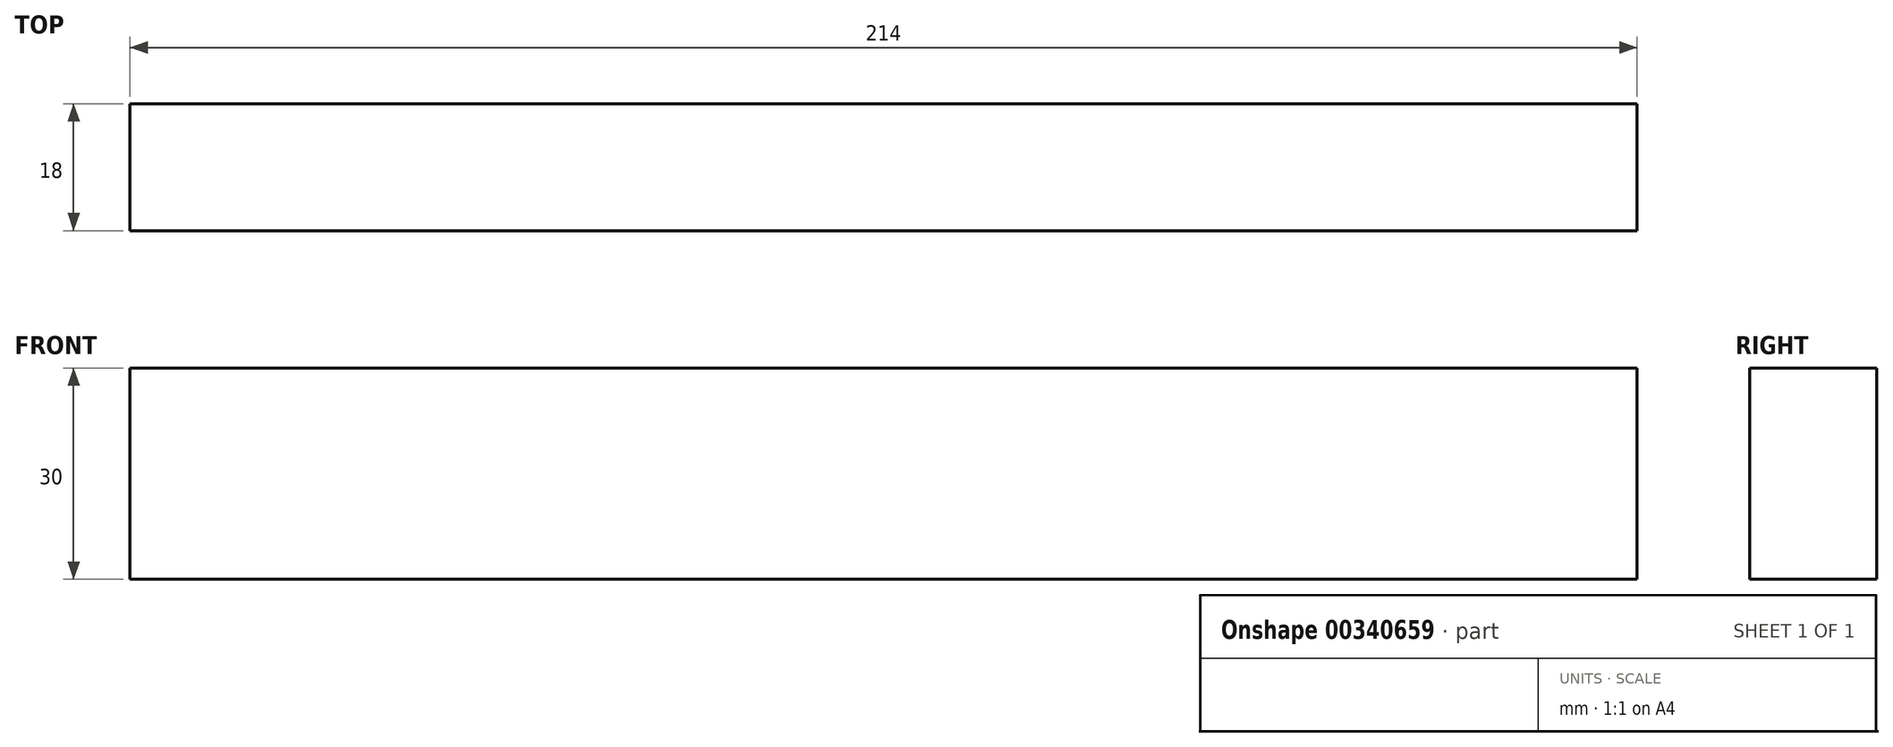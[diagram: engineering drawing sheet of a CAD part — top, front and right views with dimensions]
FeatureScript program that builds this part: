
annotation { "Feature Type Name" : "Feature", "Feature Type Description" : "" }
export const myFeature = defineFeature(function(context is Context, id is Id, definition is map)
    precondition{}
    {
        {
            var Q0;
            Q0=qCreatedBy(makeId("Front.planeOp"),FACE);
            var sketch = newSketch(context, id + "F0", { "sketchPlane" : qUnion([Q0])});
            skLineSegment(sketch, "E0.bottom", {"start": v(-94.9, -7.3) * mm, "end": v(119.1, -7.3) * mm});
            skLineSegment(sketch, "E0.top", {"start": v(-94.9, -37.3) * mm, "end": v(119.1, -37.3) * mm});
            skLineSegment(sketch, "E0.left", {"start": v(-94.9, -7.3) * mm, "end": v(-94.9, -37.3) * mm});
            skLineSegment(sketch, "E0.right", {"start": v(119.1, -7.3) * mm, "end": v(119.1, -37.3) * mm});
            skSolve(sketch);
        }
        {
            var Q0;
            Q0=makeQuery(id+"F0.imprint","IMPRINT",FACE,{"disambiguationData":[TD([[makeQuery(id+"F0.imprint","IMPRINT",EDGE,{"derivedFrom":sQuery(id+"F0.wireOp",EDGE,"E0.bottom")}),-1.0]])]});
            extrude(context, id + "F1", {"entities" : qUnion([Q0]), "depth" : 18 * mm});
        }
    });
